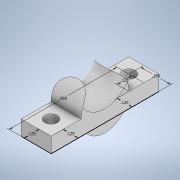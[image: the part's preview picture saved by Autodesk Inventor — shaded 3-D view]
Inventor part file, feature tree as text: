
AUTODESK INVENTOR PART (.ipt)
format: ipt  version: 2020 (Build 240168000, 168)  size: 155,648 bytes
history: native  units: in
note: dims shown in document units (in); Inventor stores cm internally (conversion verified against a paired STEP export)
features: sketch x2, extrude x2, hole x1, fillet x1
ambient origin geometry x8: Origin, YZ Plane, XZ Plane, XY Plane, X Axis, Y Axis, Z Axis, Center Point
bodies: Solid1 (feature_tree)
feature tree (6):
  sketch  "Sketch1"  dims[d0=0.25in d1=0.9in]
  extrude  "Extrusion1"  Depth=0.9in
  hole  "Hole1"  [1 undecoded]
  extrude  "Extrusion2"  Depth=0.125in
  fillet  "Fillet1"  Radius=0.125in
  sketch  "Sketch2"  dims[d2=0.125in d3=0.125in d4=0.125in d5=0.125in d6=0.125in d7=0.0in d8=0.1065in d9=0.75in d10=0.375in d11=0.25in d12=0.5635in d13=0.25in d14=0.0in d15=0.4in d16=0.2in d17=0.25in d18=0.0in d19=0.125in]
note: 1 required parameter value undecoded (feature->parameter linkage not recoverable at this tier; creation-order binding heuristic only, values carry confidence <= 0.55)
